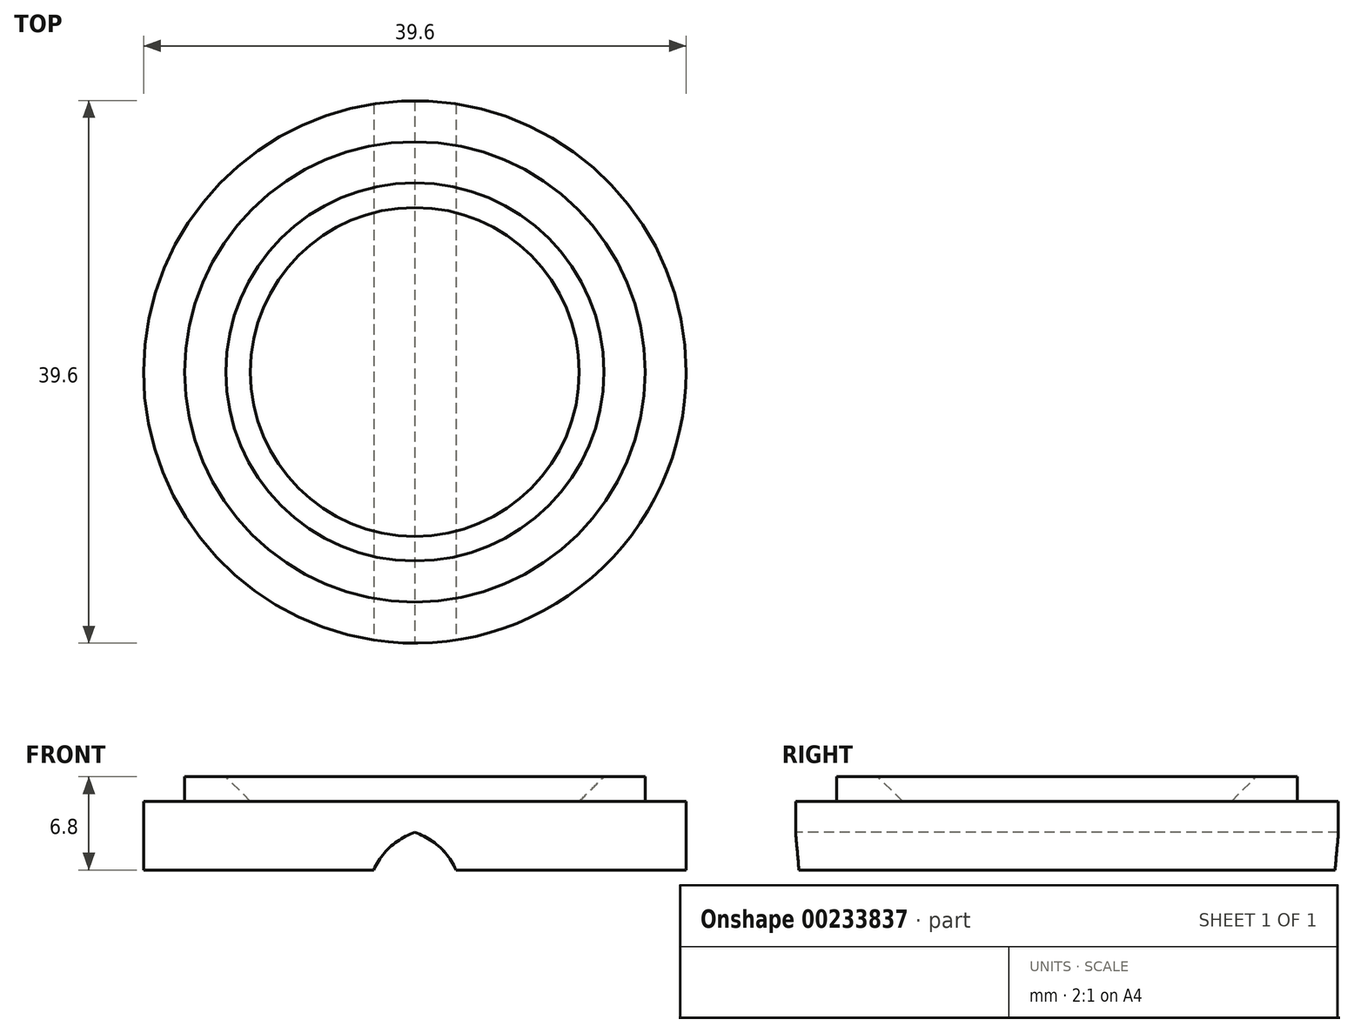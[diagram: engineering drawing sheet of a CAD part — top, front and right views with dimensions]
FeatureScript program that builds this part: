
annotation { "Feature Type Name" : "Feature", "Feature Type Description" : "" }
export const myFeature = defineFeature(function(context is Context, id is Id, definition is map)
    precondition{}
    {
        {
            var Q0;
            Q0=qCreatedBy(makeId("Top.planeOp"),FACE);
            var sketch = newSketch(context, id + "F0", { "sketchPlane" : qUnion([Q0])});
            skCircle(sketch, "E0", {"center": v(0, 0) * mm, "radius": 19.8 * mm});
            skSolve(sketch);
        }
        {
            var Q0;
            Q0 = qSketchRegion(id + "F0", true);
            extrude(context, id + "F1", {"entities" : qUnion([Q0]), "depth" : 5 * mm});
        }
        {
            var Q0;
            Q0=makeQuery(id+"F1.opExtrude","CAP_FACE",FACE,{"disambiguationData":[OSD([sQuery(id+"F0.wireOp",EDGE,"E0")])],"isStart":false});
            var sketch = newSketch(context, id + "F2", { "sketchPlane" : qUnion([Q0])});
            skCircle(sketch, "E1", {"center": v(0, 0) * mm, "radius": 16.8 * mm});
            skCircle(sketch, "E2", {"center": v(0, 0) * mm, "radius": 16 * mm});
            skSolve(sketch);
        }
        {
            var Q0;
            Q0 = qSketchRegion(id + "F2", true);
            extrude(context, id + "F3", {"entities" : qUnion([Q0]), "operationType" : NewBodyOperationType.ADD, "depth" : 1.8 * mm});
        }
        {
            var Q0;
            Q0=makeQuery(id+"F3.opExtrude","CAP_EDGE",EDGE,{"disambiguationData":[OSD([sQuery(id+"F2.wireOp",EDGE,"E2")])],"isStart":true});
            chamfer(context, id + "F4", {"entities" : qUnion([Q0]), "width" : 4 * mm, "tangentPropagation" : true});
        }
        {
            var Q0;
            Q0=makeQuery(id+"F1.opExtrude","CAP_FACE",FACE,{"disambiguationData":[OSD([sQuery(id+"F0.wireOp",EDGE,"E0")])],"isStart":true});
            var sketch = newSketch(context, id + "F5", { "sketchPlane" : qUnion([Q0])});
            skLineSegment(sketch, "E3", {"start": v(0, -25.24) * mm, "end": v(0, 37.81) * mm, "construction": true});
            skLineSegment(sketch, "E4", {"start": v(-3, -19.57) * mm, "end": v(-3, 19.57) * mm});
            skCircle(sketch, "E5.0", {"center": v(0, 0) * mm, "radius": 19.8 * mm});
            skLineSegment(sketch, "E6.MirrorCS", {"start": v(3, -19.57) * mm, "end": v(3, 19.57) * mm});
            skSolve(sketch);
        }
        {
            var Q0;
            {var subQ0=sQuery(id+"F5.wireOp",EDGE,"E4");Q0=makeQuery(id+"F5.imprint","IMPRINT",FACE,{"disambiguationData":[TD([[makeQuery(id+"F5.imprint","IMPRINT",EDGE,{"derivedFrom":subQ0}),-1.0]])]});}
            extrude(context, id + "F6", {"entities" : qUnion([Q0]), "operationType" : NewBodyOperationType.REMOVE, "oppositeDirection" : true, "depth" : 3 * mm});
        }
        {
            var Q0;
            Q0=makeQuery(id+"F6.boolean.opBoolean","COPY",EDGE,{"derivedFrom":makeQuery(id+"F6.opExtrude","CAP_EDGE",EDGE,{"disambiguationData":[OSD([sQuery(id+"F5.wireOp",EDGE,"E6.MirrorCS")])],"isStart":false})});
            var Q1;
            Q1=makeQuery(id+"F6.boolean.opBoolean","COPY",EDGE,{"derivedFrom":makeQuery(id+"F6.opExtrude","CAP_EDGE",EDGE,{"disambiguationData":[OSD([sQuery(id+"F5.wireOp",EDGE,"E4")])],"isStart":false})});
            fillet(context, id + "F7", {"entities" : qUnion([Q0, Q1]), "radius" : 5 * mm, "tangentPropagation" : true, "allowEdgeOverflow" : false});
        }
    });
